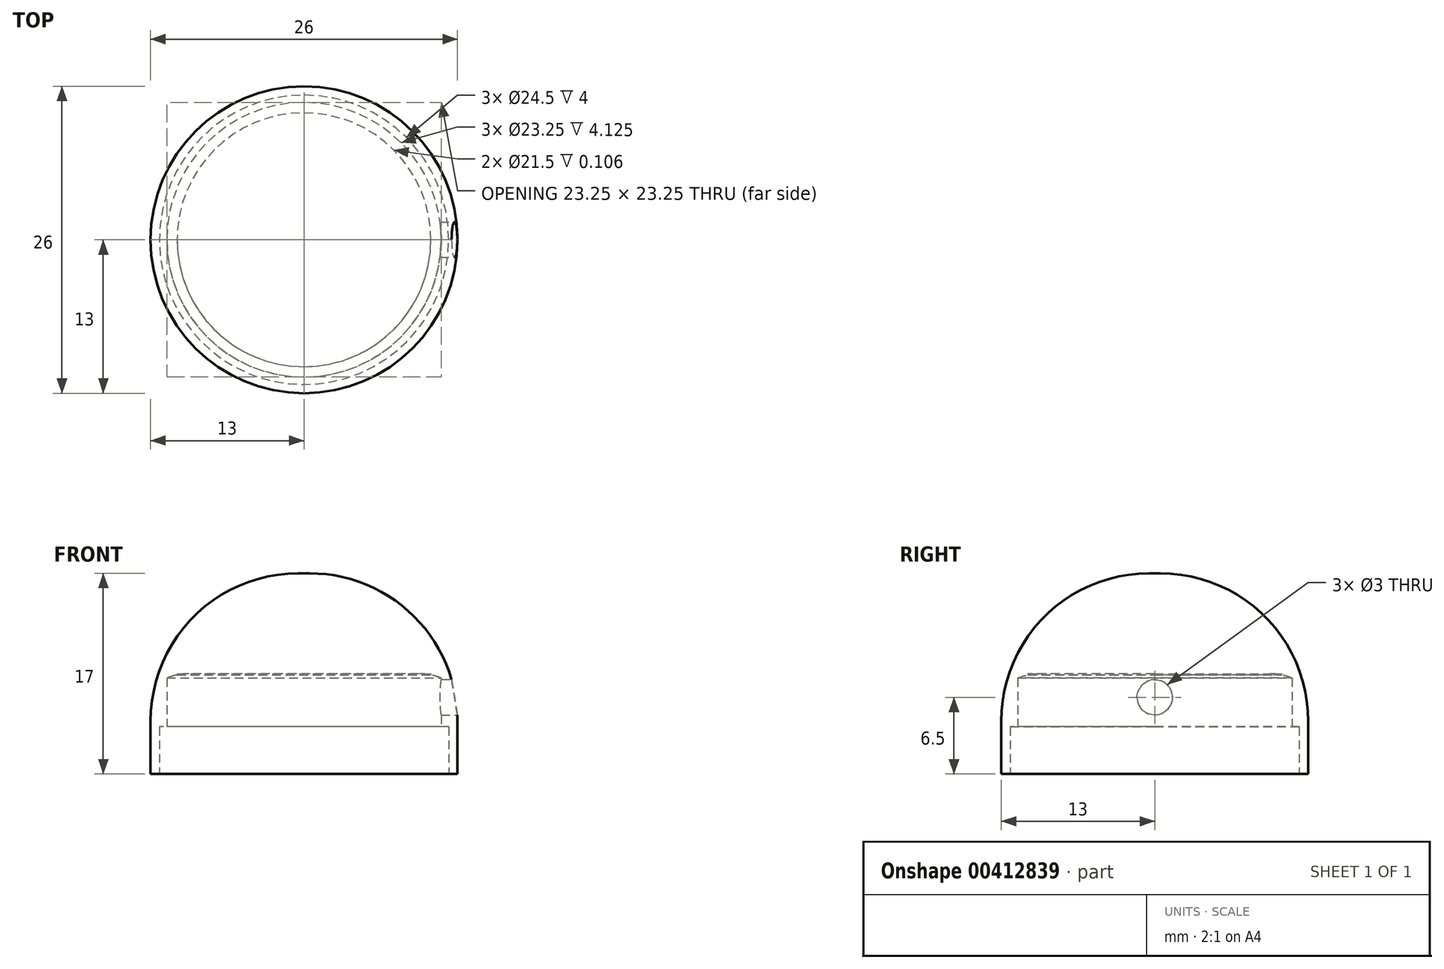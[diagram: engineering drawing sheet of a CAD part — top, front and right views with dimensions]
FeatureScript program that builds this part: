
annotation { "Feature Type Name" : "Feature", "Feature Type Description" : "" }
export const myFeature = defineFeature(function(context is Context, id is Id, definition is map)
    precondition{}
    {
        {
            var Q0;
            Q0=qCreatedBy(makeId("Top.planeOp"),FACE);
            var sketch = newSketch(context, id + "F0", { "sketchPlane" : qUnion([Q0])});
            skCircle(sketch, "E0", {"center": v(0, 0) * mm, "radius": 13 * mm});
            skSolve(sketch);
        }
        {
            var Q0;
            Q0 = qSketchRegion(id + "F0", true);
            extrude(context, id + "F1", {"entities" : qUnion([Q0]), "depth" : 15 * mm, "offsetDistance" : 25 * mm, "hasSecondDirection" : true, "secondDirectionOppositeDirection" : true, "secondDirectionDepth" : 2 * mm});
        }
        {
            var Q0;
            Q0=makeQuery(id+"F1.opExtrude","CAP_EDGE",EDGE,{"disambiguationData":[OSD([sQuery(id+"F0.wireOp",EDGE,"E0")])],"isStart":false});
            fillet(context, id + "F2", {"entities" : qUnion([Q0]), "radius" : 12.5 * mm, "tangentPropagation" : true, "allowEdgeOverflow" : false});
        }
        {
            var Q0;
            Q0=qCreatedBy(makeId("Top.planeOp"),FACE);
            var sketch = newSketch(context, id + "F3", { "sketchPlane" : qUnion([Q0])});
            skCircle(sketch, "E1", {"center": v(0, 0) * mm, "radius": 12.25 * mm});
            skSolve(sketch);
        }
        {
            var Q0;
            Q0=makeQuery(id+"F3.imprint","IMPRINT",FACE,{"disambiguationData":[TD([[makeQuery(id+"F3.imprint","IMPRINT",EDGE,{"derivedFrom":sQuery(id+"F3.wireOp",EDGE,"E1")}),1.0]])]});
            extrude(context, id + "F4", {"entities" : qUnion([Q0]), "operationType" : NewBodyOperationType.REMOVE, "depth" : 2 * mm, "offsetDistance" : 25 * mm, "hasSecondDirection" : true, "secondDirectionOppositeDirection" : true, "secondDirectionDepth" : 2 * mm});
        }
        {
            var Q0;
            Q0=qCreatedBy(makeId("Top.planeOp"),FACE);
            var sketch = newSketch(context, id + "F5", { "sketchPlane" : qUnion([Q0])});
            skCircle(sketch, "E2", {"center": v(0, 0) * mm, "radius": 11.63 * mm});
            skSolve(sketch);
        }
        {
            var Q0;
            Q0 = qSketchRegion(id + "F5", true);
            extrude(context, id + "F6", {"entities" : qUnion([Q0]), "operationType" : NewBodyOperationType.REMOVE, "depth" : 6 * mm, "offsetDistance" : 25 * mm});
        }
        {
            var Q0;
            Q0=qCreatedBy(makeId("Top.planeOp"),FACE);
            var sketch = newSketch(context, id + "F7", { "sketchPlane" : qUnion([Q0])});
            skCircle(sketch, "E3", {"center": v(0, 0) * mm, "radius": 10.75 * mm});
            skSolve(sketch);
        }
        {
            var Q0;
            Q0=makeQuery(id+"F7.imprint","IMPRINT",FACE,{"disambiguationData":[TD([[makeQuery(id+"F7.imprint","IMPRINT",EDGE,{"derivedFrom":sQuery(id+"F7.wireOp",EDGE,"E3")}),1.0]])]});
            extrude(context, id + "F8", {"entities" : qUnion([Q0]), "operationType" : NewBodyOperationType.REMOVE, "depth" : 6.5 * mm, "offsetDistance" : 25 * mm});
        }
        {
            var Q0;
            Q0=makeQuery(id+"F8.boolean.opBoolean","INTERSECT",EDGE,{"derivedFrom":[makeQuery(id+"F6.boolean.opBoolean","COPY",FACE,{"derivedFrom":makeQuery(id+"F6.opExtrude","CAP_FACE",FACE,{"disambiguationData":[OSD([sQuery(id+"F5.wireOp",EDGE,"E2")])],"isStart":false})}),makeQuery(id+"F8.opExtrude","SWEPT_FACE",FACE,{"disambiguationData":[OSD([sQuery(id+"F7.wireOp",EDGE,"E3")])]})]});
            chamfer(context, id + "F9", {"entities" : qUnion([Q0]), "width" : 1 * mm, "tangentPropagation" : true});
        }
        {
            var Q0;
            {var subQ0=sQuery(id+"F7.wireOp",EDGE,"E3");Q0=makeQuery(id+"F9.opChamfer","BLEND_EDGE",EDGE,{"blendedFrom":[makeQuery(id+"F8.boolean.opBoolean","INTERSECT",EDGE,{"derivedFrom":[makeQuery(id+"F6.boolean.opBoolean","COPY",FACE,{"derivedFrom":makeQuery(id+"F6.opExtrude","CAP_FACE",FACE,{"disambiguationData":[OSD([sQuery(id+"F5.wireOp",EDGE,"E2")])],"isStart":false})}),makeQuery(id+"F8.opExtrude","SWEPT_FACE",FACE,{"disambiguationData":[OSD([subQ0])]})]}),makeQuery(id+"F8.boolean.opBoolean","COPY",FACE,{"derivedFrom":makeQuery(id+"F8.opExtrude","CAP_FACE",FACE,{"disambiguationData":[OSD([subQ0])],"isStart":false})})],"blendedInto":[makeQuery(id+"F8.boolean.opBoolean","COPY",FACE,{"derivedFrom":makeQuery(id+"F8.opExtrude","CAP_FACE",FACE,{"disambiguationData":[OSD([subQ0])],"isStart":false})})]});}
            fillet(context, id + "F10", {"entities" : qUnion([Q0]), "radius" : 5 * mm, "tangentPropagation" : true, "allowEdgeOverflow" : false});
        }
        {
            var Q0;
            Q0=qCreatedBy(makeId("Right.planeOp"),FACE);
            cPlane(context, id + "F11", {"entities" : qUnion([Q0]), "cplaneType" : CPlaneType.OFFSET, "offset" : 13 * mm, "width" : 150 * mm, "height" : 150 * mm});
        }
        {
            var Q0;
            Q0=qCreatedBy(id+"F11.planeOp",FACE);
            var sketch = newSketch(context, id + "F12", { "sketchPlane" : qUnion([Q0])});
            skCircle(sketch, "E4", {"center": v(0, 4.5) * mm, "radius": 1.5 * mm});
            skSolve(sketch);
        }
        {
            var Q0;
            Q0=makeQuery(id+"F12.imprint","IMPRINT",FACE,{"disambiguationData":[TD([[makeQuery(id+"F12.imprint","IMPRINT",EDGE,{"derivedFrom":sQuery(id+"F12.wireOp",EDGE,"E4")}),1.0]])]});
            extrude(context, id + "F13", {"entities" : qUnion([Q0]), "operationType" : NewBodyOperationType.REMOVE, "oppositeDirection" : true, "depth" : 20 * mm, "offsetDistance" : 25 * mm});
        }
    });
